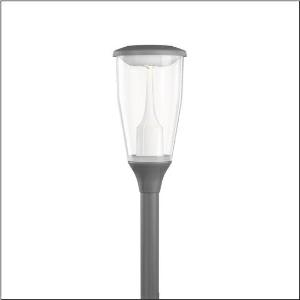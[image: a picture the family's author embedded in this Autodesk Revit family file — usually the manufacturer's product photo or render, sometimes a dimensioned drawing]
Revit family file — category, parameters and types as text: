
# Revit family: dl_11_iq___st1_2a_5xa5565af14hp00022_6a76
name_source: partatom
category: Lighting Fixtures
units: mm (PartAtom-declared; Revit-internal decimal feet)

## family parameters
Cut with Voids When Loaded = No
Host = Face
Light Source = No
Part Type = Normal
Room Calculation Point = No
Round Connector Dimension = Use Diameter
Shared = No

## types (1)
- --- (1 x LED, 4000 lm, 33.6 W, 2200K)
    Apparent Load = 34 VA
    CIE Flux Codes = 33 63 91 94 100
    Color Rendering = 70
    Color Temperature = 2200K
    Default Elevation = 1800 mm
    Description = DL 11 iQ, mast luminaire, Module 540 iQ-SR, primary light control with 3 zone facetted reflector, of plastic, silver coated, highly specular, structured, primary optical cover: cover, of PMMA, transparent, light distribution: ST1.2a, light emission: direct distribution, primary light characteristic: asymmetric, installation type: post-top, LED, High Power LED, light colour: 722, colour temperature: 2200K, control: Street-Remote, Auto-Match, Temp-Guard, Lumen-Switch, Night-Set, Smart-Wire, Light-Fading, Desk-Remote (wireless, voltage-free reading and setting of iQ features in the workshop via application-optimized NFC function/RFID function), optimised constant luminous flux control (CLO 2.0), mains connection: 220..240V, AC, 50/60Hz, connection cable pre-assembled, cable length: 5,5m, luminaire housing, upper part, of diecast aluminium, coated, Siteco® metallic grey (DB 702S), spigot size: 60mm (post-top), post-top mast mounting element, of diecast aluminium, coated, Siteco® metallic grey (DB 702S), Module 540 iQ-SR, traffic white (RAL 9016), equipment: Power, protection rating (complete): IP66, insulation class (complete): insulation class II (safety insulation), certification: CE, ENEC, ENEC+, VDE, packaging unit: 1 piece

Light Distribution: ST1.2a
    Height = 665 mm
    Lamp = 1 x LED
    Lamp Light Flux = 4000 lm
    Lamp Power = 33.6 W
    Lamp count = 1
    Length = 334 mm
    Luminous efficacy = 119 lm/W
    Manufacturer = Siteco
    ModVariant = No
    Model = 5XA5565AF14HP00022
    Number of Poles = 1
    OnlyDefault = Yes
    Power Factor = 1
    Product Name = DL 11 iQ | ST1.2a
    Product group = mast luminaire | pylon top
    ProductGroupID = 6100
    Protection Class = Protection class II
    Protection Degree = IP 66
    RLX_Detail_Level = 1
    RLX_Emergency_Light_Flux = 0 lm
    RLX_Emergency_Type = 0
    RLX_Emergency_Type_DB = No
    RlxData = <blob elided: 97213 chars, md5=88520e8d>
    Socket = socket
    Standby Power = 0 W
    System Light Flux = 4000 lm
    System Power = 34 W
    Type Comments = factory setting: luminous flux: 100 % | dim-lin: 254 | 695 mA
    Type Image = l_1258354.jpg
    URL = http://relux.com
    VarID = @adj_002727
    Voltage = 0 V
    Weight = 0.00 kg
    Width = 0 mm  [stored 0 ft]

note: [stored X ft] marks values corroborated as IEEE doubles in the binary element streams (Revit-internal decimal feet)

## geometry (parser evidence)
native form markers: Blend x4, Sweep x11
no freeform markers — native parametric forms only
